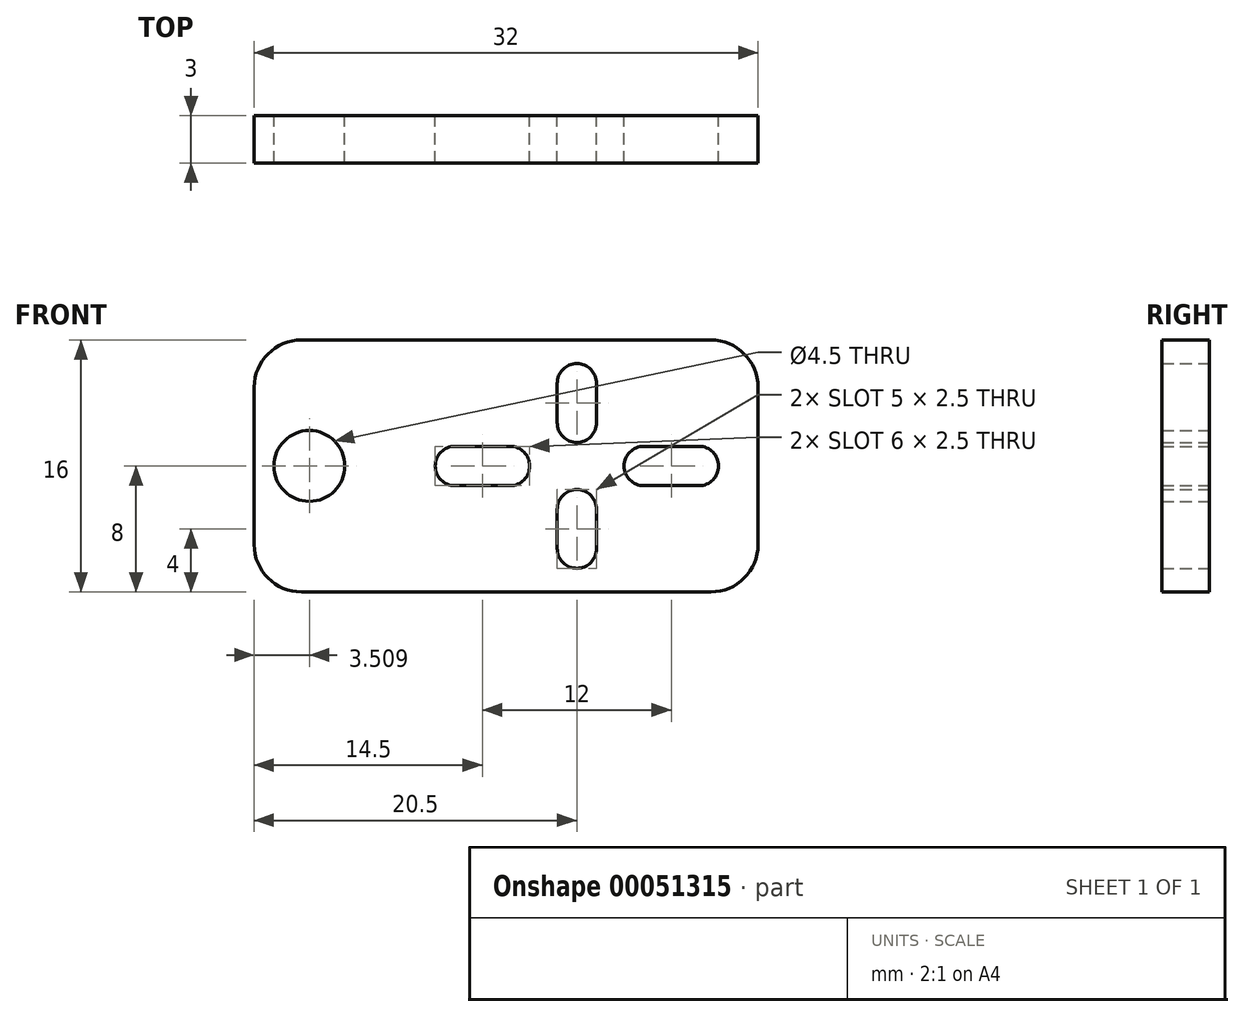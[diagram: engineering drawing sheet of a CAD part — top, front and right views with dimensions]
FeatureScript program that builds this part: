
annotation { "Feature Type Name" : "Feature", "Feature Type Description" : "" }
export const myFeature = defineFeature(function(context is Context, id is Id, definition is map)
    precondition{}
    {
        {
            var Q0;
            Q0=qCreatedBy(makeId("Front.planeOp"),FACE);
            var sketch = newSketch(context, id + "F0", { "sketchPlane" : qUnion([Q0])});
            skLineSegment(sketch, "E0.bottom", {"start": v(0, 0) * mm, "end": v(32, 0) * mm});
            skLineSegment(sketch, "E0.top", {"start": v(0, 16) * mm, "end": v(32, 16) * mm});
            skLineSegment(sketch, "E0.left", {"start": v(0, 0) * mm, "end": v(0, 16) * mm});
            skLineSegment(sketch, "E0.right", {"start": v(32, 0) * mm, "end": v(32, 16) * mm});
            skLineSegment(sketch, "E1", {"start": v(0, 8) * mm, "end": v(32, 8) * mm, "construction": true});
            skLineSegment(sketch, "E2", {"start": v(16, 16) * mm, "end": v(16, 0) * mm, "construction": true});
            skCircle(sketch, "E3", {"center": v(3.5, 8) * mm, "radius": 2.25 * mm});
            skLineSegment(sketch, "E4.bottom", {"start": v(24.75, 9.25) * mm, "end": v(28.25, 9.25) * mm});
            skLineSegment(sketch, "E4.top", {"start": v(24.75, 6.75) * mm, "end": v(28.25, 6.75) * mm});
            skLineSegment(sketch, "E4.left", {"start": v(23.5, 8) * mm, "end": v(23.5, 8) * mm});
            skLineSegment(sketch, "E4.right", {"start": v(29.5, 8) * mm, "end": v(29.5, 8) * mm});
            skLineSegment(sketch, "E5.bottom", {"start": v(12.75, 9.25) * mm, "end": v(16.25, 9.25) * mm});
            skLineSegment(sketch, "E5.top", {"start": v(12.75, 6.75) * mm, "end": v(16.25, 6.75) * mm});
            skLineSegment(sketch, "E5.left", {"start": v(11.5, 8) * mm, "end": v(11.5, 8) * mm});
            skLineSegment(sketch, "E5.right", {"start": v(17.5, 8) * mm, "end": v(17.5, 8) * mm});
            skLineSegment(sketch, "E6.bottom", {"start": v(20.5, 14.5) * mm, "end": v(20.5, 14.5) * mm});
            skLineSegment(sketch, "E6.top", {"start": v(20.5, 9.5) * mm, "end": v(20.5, 9.5) * mm});
            skLineSegment(sketch, "E6.left", {"start": v(19.25, 13.25) * mm, "end": v(19.25, 10.75) * mm});
            skLineSegment(sketch, "E6.right", {"start": v(21.75, 13.25) * mm, "end": v(21.75, 10.75) * mm});
            skLineSegment(sketch, "E7.bottom", {"start": v(20.5, 6.5) * mm, "end": v(20.5, 6.5) * mm});
            skLineSegment(sketch, "E7.top", {"start": v(20.5, 1.5) * mm, "end": v(20.5, 1.5) * mm});
            skLineSegment(sketch, "E7.left", {"start": v(19.25, 5.25) * mm, "end": v(19.25, 2.75) * mm});
            skLineSegment(sketch, "E7.right", {"start": v(21.75, 5.25) * mm, "end": v(21.75, 2.75) * mm});
            skPoint(sketch, "E8.visualSharp", {"position": v(19.25, 14.5) * mm});
            skArc(sketch, "E8.filletArc", {"start": v(20.5, 14.5) * mm, "mid": v(19.62, 14.13) * mm, "end": v(19.25, 13.25) * mm});
            skPoint(sketch, "E9.visualSharp", {"position": v(19.25, 9.5) * mm});
            skArc(sketch, "E9.filletArc", {"start": v(19.25, 10.75) * mm, "mid": v(19.62, 9.87) * mm, "end": v(20.5, 9.5) * mm});
            skPoint(sketch, "E10.visualSharp", {"position": v(21.75, 14.5) * mm});
            skArc(sketch, "E10.filletArc", {"start": v(21.75, 13.25) * mm, "mid": v(21.38, 14.13) * mm, "end": v(20.5, 14.5) * mm});
            skPoint(sketch, "E11.visualSharp", {"position": v(21.75, 9.5) * mm});
            skArc(sketch, "E11.filletArc", {"start": v(20.5, 9.5) * mm, "mid": v(21.38, 9.87) * mm, "end": v(21.75, 10.75) * mm});
            skPoint(sketch, "E12.visualSharp", {"position": v(11.5, 9.25) * mm});
            skArc(sketch, "E12.filletArc", {"start": v(12.75, 9.25) * mm, "mid": v(11.87, 8.88) * mm, "end": v(11.5, 8) * mm});
            skPoint(sketch, "E13.visualSharp", {"position": v(17.5, 9.25) * mm});
            skArc(sketch, "E13.filletArc", {"start": v(17.5, 8) * mm, "mid": v(17.13, 8.88) * mm, "end": v(16.25, 9.25) * mm});
            skPoint(sketch, "E14.visualSharp", {"position": v(11.5, 6.75) * mm});
            skArc(sketch, "E14.filletArc", {"start": v(11.5, 8) * mm, "mid": v(11.87, 7.12) * mm, "end": v(12.75, 6.75) * mm});
            skPoint(sketch, "E15.visualSharp", {"position": v(17.5, 6.75) * mm});
            skArc(sketch, "E15.filletArc", {"start": v(16.25, 6.75) * mm, "mid": v(17.13, 7.12) * mm, "end": v(17.5, 8) * mm});
            skPoint(sketch, "E16.visualSharp", {"position": v(23.5, 6.75) * mm});
            skArc(sketch, "E16.filletArc", {"start": v(23.5, 8) * mm, "mid": v(23.87, 7.12) * mm, "end": v(24.75, 6.75) * mm});
            skPoint(sketch, "E17.visualSharp", {"position": v(23.5, 9.25) * mm});
            skArc(sketch, "E17.filletArc", {"start": v(24.75, 9.25) * mm, "mid": v(23.87, 8.88) * mm, "end": v(23.5, 8) * mm});
            skPoint(sketch, "E18.visualSharp", {"position": v(29.5, 9.25) * mm});
            skArc(sketch, "E18.filletArc", {"start": v(29.5, 8) * mm, "mid": v(29.13, 8.88) * mm, "end": v(28.25, 9.25) * mm});
            skPoint(sketch, "E19.visualSharp", {"position": v(29.5, 6.75) * mm});
            skArc(sketch, "E19.filletArc", {"start": v(28.25, 6.75) * mm, "mid": v(29.13, 7.12) * mm, "end": v(29.5, 8) * mm});
            skPoint(sketch, "E20.visualSharp", {"position": v(19.25, 1.5) * mm});
            skArc(sketch, "E20.filletArc", {"start": v(19.25, 2.75) * mm, "mid": v(19.62, 1.87) * mm, "end": v(20.5, 1.5) * mm});
            skPoint(sketch, "E21.visualSharp", {"position": v(21.75, 1.5) * mm});
            skArc(sketch, "E21.filletArc", {"start": v(20.5, 1.5) * mm, "mid": v(21.38, 1.87) * mm, "end": v(21.75, 2.75) * mm});
            skPoint(sketch, "E22.visualSharp", {"position": v(19.25, 6.5) * mm});
            skArc(sketch, "E22.filletArc", {"start": v(20.5, 6.5) * mm, "mid": v(19.62, 6.13) * mm, "end": v(19.25, 5.25) * mm});
            skPoint(sketch, "E23.visualSharp", {"position": v(21.75, 6.5) * mm});
            skArc(sketch, "E23.filletArc", {"start": v(21.75, 5.25) * mm, "mid": v(21.38, 6.13) * mm, "end": v(20.5, 6.5) * mm});
            skSolve(sketch);
        }
        {
            var Q0;
            Q0=makeQuery(id+"F0.imprint","IMPRINT",FACE,{"disambiguationData":[TD([[makeQuery(id+"F0.imprint","IMPRINT",EDGE,{"derivedFrom":sQuery(id+"F0.wireOp",EDGE,"E0.bottom")}),1.0]])]});
            extrude(context, id + "F1", {"entities" : qUnion([Q0]), "depth" : 3 * mm});
        }
        {
            var Q0;
            Q0=makeQuery(id+"F1.opExtrude","SWEPT_EDGE",EDGE,{"disambiguationData":[OSD([sQuery(id+"F0.wireOp",EDGE,"E0.bottom"),sQuery(id+"F0.wireOp",EDGE,"E0.right")])]});
            var Q1;
            Q1=makeQuery(id+"F1.opExtrude","SWEPT_EDGE",EDGE,{"disambiguationData":[OSD([sQuery(id+"F0.wireOp",EDGE,"E0.top"),sQuery(id+"F0.wireOp",EDGE,"E0.right")])]});
            var Q2;
            Q2=makeQuery(id+"F1.opExtrude","SWEPT_EDGE",EDGE,{"disambiguationData":[OSD([sQuery(id+"F0.wireOp",EDGE,"E0.bottom"),sQuery(id+"F0.wireOp",EDGE,"E0.left")])]});
            var Q3;
            Q3=makeQuery(id+"F1.opExtrude","SWEPT_EDGE",EDGE,{"disambiguationData":[OSD([sQuery(id+"F0.wireOp",EDGE,"E0.top"),sQuery(id+"F0.wireOp",EDGE,"E0.left")])]});
            fillet(context, id + "F2", {"entities" : qUnion([Q0, Q1, Q2, Q3]), "radius" : 3 * mm, "tangentPropagation" : true, "allowEdgeOverflow" : false});
        }
    });
